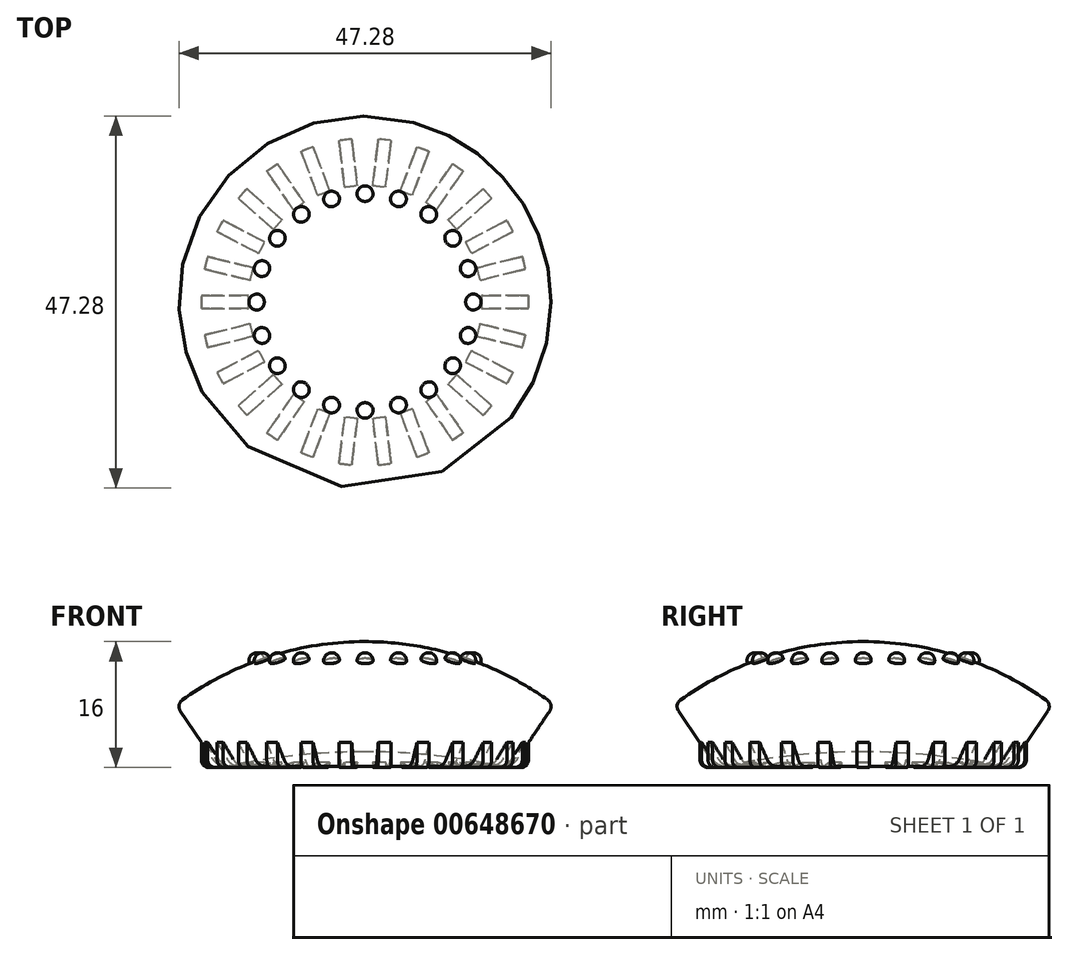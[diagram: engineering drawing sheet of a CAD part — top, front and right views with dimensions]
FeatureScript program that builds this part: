
annotation { "Feature Type Name" : "Feature", "Feature Type Description" : "" }
export const myFeature = defineFeature(function(context is Context, id is Id, definition is map)
    precondition{}
    {
        {
            var Q0;
            Q0=qCreatedBy(makeId("Front.planeOp"),FACE);
            var sketch = newSketch(context, id + "F0", { "sketchPlane" : qUnion([Q0])});
            skArc(sketch, "E0", {"start": v(23.22, 0.57) * mm, "mid": v(0, 8) * mm, "end": v(-23.22, 0.57) * mm});
            skLineSegment(sketch, "E1", {"start": v(-23.47, -0.8) * mm, "end": v(-19.35, -6.94) * mm});
            skLineSegment(sketch, "E2", {"start": v(19.35, -6.94) * mm, "end": v(23.47, -0.8) * mm});
            skArc(sketch, "E3", {"start": v(17.28, -7.79) * mm, "mid": v(0, -6) * mm, "end": v(-17.28, -7.79) * mm});
            skLineSegment(sketch, "E4", {"start": v(0, 20.88) * mm, "end": v(0, -23.57) * mm});
            skPoint(sketch, "E5.visualSharp", {"position": v(-24, 0) * mm});
            skArc(sketch, "E5.filletArc", {"start": v(-23.22, 0.57) * mm, "mid": v(-23.62, -0.06) * mm, "end": v(-23.47, -0.8) * mm});
            skPoint(sketch, "E6.visualSharp", {"position": v(24, 0) * mm});
            skArc(sketch, "E6.filletArc", {"start": v(23.47, -0.8) * mm, "mid": v(23.62, -0.06) * mm, "end": v(23.22, 0.57) * mm});
            skPoint(sketch, "E7.visualSharp", {"position": v(-18.6, -8.08) * mm});
            skArc(sketch, "E7.filletArc", {"start": v(-19.35, -6.94) * mm, "mid": v(-18.44, -7.68) * mm, "end": v(-17.28, -7.79) * mm});
            skPoint(sketch, "E8.visualSharp", {"position": v(18.6, -8.08) * mm});
            skArc(sketch, "E8.filletArc", {"start": v(17.28, -7.79) * mm, "mid": v(18.44, -7.68) * mm, "end": v(19.35, -6.94) * mm});
            skLineSegment(sketch, "E9", {"start": v(0, 8) * mm, "end": v(0, 0) * mm});
            skLineSegment(sketch, "E10", {"start": v(0, 0) * mm, "end": v(0, -6) * mm});
            skLineSegment(sketch, "E11", {"start": v(13.87, 5.52) * mm, "end": v(7.84, -6.36) * mm});
            skSolve(sketch);
        }
        {
            var Q0;
            {var subQ0=sQuery(id+"F0.wireOp",EDGE,"E1");Q0=makeQuery(id+"F0.imprint","IMPRINT",FACE,{"disambiguationData":[TD([[makeQuery(id+"F0.imprint","IMPRINT",EDGE,{"derivedFrom":subQ0}),1.0]])]});}
            var Q1;
            Q1=sQuery(id+"F0.wireOp",EDGE,"E4");
            revolve(context, id + "F1", {"entities" : qUnion([Q0]), "axis" : qUnion([Q1]), "revolveType" : RevolveType.FULL});
        }
        {
            var Q0;
            Q0=qCreatedBy(makeId("Top.planeOp"),FACE);
            var sketch = newSketch(context, id + "F2", { "sketchPlane" : qUnion([Q0])});
            skLineSegment(sketch, "E12.bottom", {"start": v(-14.77, -0.82) * mm, "end": v(-20.78, -0.82) * mm});
            skLineSegment(sketch, "E12.top", {"start": v(-14.77, 0.82) * mm, "end": v(-20.78, 0.82) * mm});
            skLineSegment(sketch, "E12.left", {"start": v(-14.77, -0.82) * mm, "end": v(-14.77, 0.82) * mm});
            skLineSegment(sketch, "E12.right", {"start": v(-20.78, -0.82) * mm, "end": v(-20.78, 0.82) * mm});
            skSolve(sketch);
        }
        {
            var Q0;
            Q0 = qSketchRegion(id + "F2", true);
            extrude(context, id + "F3", {"entities" : qUnion([Q0]), "oppositeDirection" : true, "depth" : 8 * mm, "offsetDistance" : 25 * mm});
        }
        {
            var Q0;
            Q0=makeQuery(id+"F3.opExtrude","CAP_EDGE",EDGE,{"disambiguationData":[OSD([sQuery(id+"F2.wireOp",EDGE,"E12.right")])],"isStart":false});
            var Q1;
            Q1=makeQuery(id+"F3.opExtrude","CAP_EDGE",EDGE,{"disambiguationData":[OSD([sQuery(id+"F2.wireOp",EDGE,"E12.left")])],"isStart":false});
            fillet(context, id + "F4", {"entities" : qUnion([Q0, Q1]), "radius" : 1 * mm, "tangentPropagation" : true, "allowEdgeOverflow" : false});
        }
        {
            var Q0;
            Q0=makeQuery(id+"F3.opExtrude","SWEPT_BODY",BODY,{"disambiguationData":[OSD([sQuery(id+"F2.wireOp",EDGE,"E12.bottom"),sQuery(id+"F2.wireOp",EDGE,"E12.top"),sQuery(id+"F2.wireOp",EDGE,"E12.left"),sQuery(id+"F2.wireOp",EDGE,"E12.right")])]});
            var Q1;
            Q1=sQuery(id+"F0.wireOp",EDGE,"E4");
            circularPattern(context, id + "F5", {"operationType" : NewBodyOperationType.ADD, "entities" : qUnion([Q0]), "axis" : qUnion([Q1]), "angle" : 360 * degree, "instanceCount" : 26, "equalSpace" : true});
        }
        {
            var Q0;
            Q0=sQuery(id+"F0.wireOp",VERTEX,"E11.start");
            var Q1;
            Q1=sQuery(id+"F0.wireOp",EDGE,"E11");
            cPlane(context, id + "F6", {"entities" : qUnion([Q0, Q1]), "cplaneType" : CPlaneType.LINE_POINT, "offset" : 25 * mm, "width" : 150 * mm, "height" : 150 * mm});
        }
        {
            var Q0;
            Q0=qCreatedBy(id+"F6.planeOp",FACE);
            var sketch = newSketch(context, id + "F7", { "sketchPlane" : qUnion([Q0])});
            skCircle(sketch, "E13", {"center": v(9.73, 0) * mm, "radius": 1 * mm});
            skLineSegment(sketch, "E14", {"start": v(10.73, 0) * mm, "end": v(8.72, 0) * mm});
            skSolve(sketch);
        }
        {
            var Q0;
            {var subQ0=sQuery(id+"F7.wireOp",EDGE,"E14");Q0=makeQuery(id+"F7.imprint","IMPRINT",FACE,{"disambiguationData":[TD([[makeQuery(id+"F7.imprint","IMPRINT",EDGE,{"derivedFrom":subQ0}),-1.0]])]});}
            var Q1;
            Q1=sQuery(id+"F7.wireOp",EDGE,"E14");
            revolve(context, id + "F8", {"entities" : qUnion([Q0]), "axis" : qUnion([Q1]), "revolveType" : RevolveType.FULL});
        }
        {
            var Q0;
            Q0=makeQuery(id+"F8.opRevolve","SWEPT_BODY",BODY,{"disambiguationData":[OSD([sQuery(id+"F7.wireOp",EDGE,"E13"),sQuery(id+"F7.wireOp",EDGE,"E14")])]});
            var Q1;
            Q1=sQuery(id+"F0.wireOp",EDGE,"E4");
            circularPattern(context, id + "F9", {"operationType" : NewBodyOperationType.ADD, "entities" : qUnion([Q0]), "axis" : qUnion([Q1]), "angle" : 360 * degree, "instanceCount" : 20, "equalSpace" : true});
        }
    });
